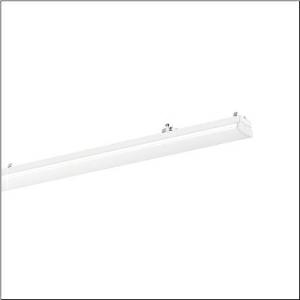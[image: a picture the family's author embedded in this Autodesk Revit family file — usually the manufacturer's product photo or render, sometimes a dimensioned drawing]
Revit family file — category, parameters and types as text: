
# Revit family: licross_11_recessed_opal_mo_51tl1d7n48xg
name_source: partatom
category: Lighting Fixtures
units: mm (PartAtom-declared; Revit-internal decimal feet)

## family parameters
Cut with Voids When Loaded = No
Host = Face
Light Source = No
Part Type = Normal
Room Calculation Point = No
Round Connector Dimension = Use Diameter
Shared = No

## types (1)
- Licross 11 recessed opal MO (1 x LED, 8490 lm, 48.5 W, 4000K)
    Apparent Load = 49 VA
    CIE Flux Codes = 44 73 91 87 100
    Color Rendering = 80
    Color Temperature = 4000K
    Default Elevation = 1800 mm
    Description = Licross 11 recessed opal MO, luminaire insert, of sheet steel, coil coated, white, length: 1.500mm, width: 76mm, height: 87mm, LED rated luminous flux: 8.490lm, light colour: 840, SDCM (Standard Deviation of Colour Matching)MacAdam ≤ 2 SDCM (initial), control gear: ON/OFF, with plug, 3-pole, with phase selection, mains connection: 220..240V, AC, 50/60Hz, rated input power: 49W, internal wiring halogen-free, primary optical cover: cover, of PMMA, light emission: direct with ceiling illumination distribution, primary light characteristic: symmetric, protection rating (complete): IP40, insulation class (complete): insulation class I (protective earthing), certification: CE, ENEC, VDE, UKCA, protection symbol: D if used in an environment without relevant dust loads with corresponding accessories, impact resistance: IK06, permissible ambient temperature for indoor applications: -35..+35°C, corresponds to IFS (International Featured Standards) requirements for safety and quality in the food industry, reducing of maximum allowable ambient temperature of 5°C with ceiling mounting, The light source and the operating device comply with the requirements of the Ecodesign Regulation (EU) 2019/2020 and are replaceable in accordance with this regulation, packaging unit: 1 piece
    Height = 83 mm
    Lamp = 1 x LED
    Lamp Light Flux = 8490 lm
    Lamp Power = 48.5 W
    Lamp count = 1
    Length = 1500 mm
    Luminous efficacy = 175 lm/W
    Manufacturer = Siteco
    ModVariant = No
    Model = 51TL1D7N48XG
    Mounting Place = Ceiling
    Mounting Type = Pendant
    Number of Poles = 1
    OnlyDefault = Yes
    Power Factor = 1
    Product Name = Licross 11 recessed opal MO
    Product group = luminaire insert | ceiling pendant
    ProductGroupID = 901
    Protection Class = Protection class I
    Protection Degree = IP 40
    RLX_Detail_Level = 1
    RLX_Emergency_Light_Flux = 0 lm
    RLX_Emergency_Type = 0
    RLX_Emergency_Type_DB = No
    RlxData = <blob elided: 23357 chars, md5=7e93957a>
    Socket = socket
    Standby Power = 0 W
    System Light Flux = 8490 lm
    System Power = 49 W
    Type Comments = Product without accessories
    Type Image = l_1313666.jpg
    URL = http://relux.com
    VarID = ---
    Voltage = 0 V
    Weight = 0.00 kg
    Width = 76 mm

## geometry (parser evidence)
native form markers: Blend x4, Sweep x14
no freeform markers — native parametric forms only
